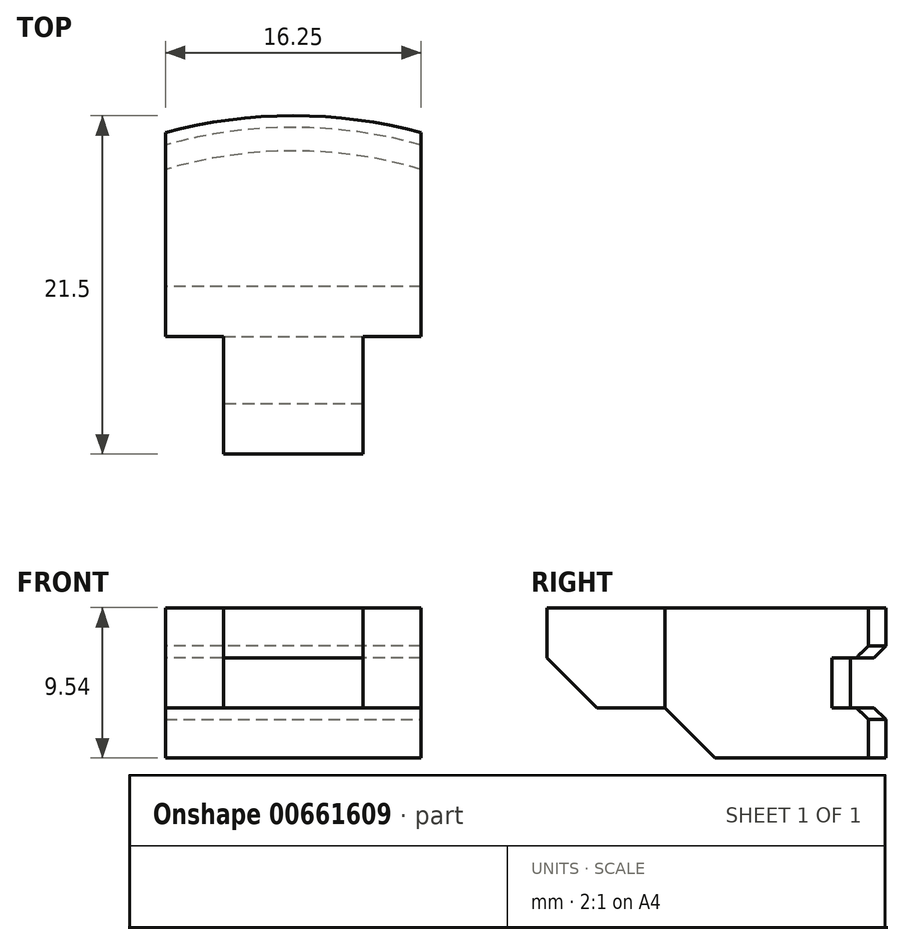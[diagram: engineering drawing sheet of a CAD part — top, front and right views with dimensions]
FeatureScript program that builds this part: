
annotation { "Feature Type Name" : "Feature", "Feature Type Description" : "" }
export const myFeature = defineFeature(function(context is Context, id is Id, definition is map)
    precondition{}
    {
        {
            var Q0;
            Q0=qCreatedBy(makeId("Top.planeOp"),FACE);
            var sketch = newSketch(context, id + "F0", { "sketchPlane" : qUnion([Q0])});
            skLineSegment(sketch, "E0.left", {"start": v(-8.12, 27.44) * mm, "end": v(-8.12, 16.84) * mm});
            skLineSegment(sketch, "E0.right", {"start": v(8.12, 27.44) * mm, "end": v(8.12, 16.84) * mm});
            skPoint(sketch, "E0.middle", {"position": v(0, 0) * mm});
            skArc(sketch, "E1", {"start": v(8.12, 27.44) * mm, "mid": v(0, 28.62) * mm, "end": v(-8.12, 27.44) * mm});
            skPoint(sketch, "E2.orphan", {"position": v(8.12, 28.62) * mm});
            skPoint(sketch, "E3.orphan", {"position": v(-8.12, 28.62) * mm});
            skPoint(sketch, "E4.orphan", {"position": v(-8.12, -28.62) * mm});
            skPoint(sketch, "E5.orphan", {"position": v(8.12, -28.62) * mm});
            skLineSegment(sketch, "E6.top", {"start": v(-8.12, 16.84) * mm, "end": v(8.12, 16.84) * mm});
            skLineSegment(sketch, "E7", {"start": v(0, 0) * mm, "end": v(0, 32.38) * mm, "construction": true});
            skPoint(sketch, "E7.endSnap0", {"position": v(0, 28.62) * mm});
            skLineSegment(sketch, "E8.bottom", {"start": v(4.43, 16.84) * mm, "end": v(0, 16.84) * mm});
            skLineSegment(sketch, "E8.top", {"start": v(4.43, 9.36) * mm, "end": v(0, 9.36) * mm});
            skLineSegment(sketch, "E8.left", {"start": v(4.43, 16.84) * mm, "end": v(4.43, 9.36) * mm});
            skLineSegment(sketch, "E8.right", {"start": v(0, 16.84) * mm, "end": v(0, 9.36) * mm});
            skLineSegment(sketch, "E9.MirrorCS", {"start": v(-4.43, 9.36) * mm, "end": v(0, 9.36) * mm});
            skLineSegment(sketch, "E10.MirrorCS", {"start": v(-4.43, 16.84) * mm, "end": v(-4.43, 9.36) * mm});
            skLineSegment(sketch, "E11.MirrorCS", {"start": v(8.12, 16.84) * mm, "end": v(-8.12, 16.84) * mm});
            skPoint(sketch, "E6.bottom.start.orphan", {"position": v(-8.12, -16.84) * mm});
            skPoint(sketch, "E12.trimOffspring.start.orphan", {"position": v(8.12, -16.84) * mm});
            skSolve(sketch);
        }
        {
            var Q0;
            Q0 = qSketchRegion(id + "F0", true);
            extrude(context, id + "F1", {"entities" : qUnion([Q0]), "oppositeDirection" : true, "depth" : 3.18 * mm, "offsetDistance" : 25 * mm});
        }
        {
            var Q0;
            Q0=makeQuery(id+"F0.imprint","IMPRINT",FACE,{"disambiguationData":[TD([[makeQuery(id+"F0.imprint","IMPRINT",EDGE,{"derivedFrom":sQuery(id+"F0.wireOp",EDGE,"E0.left")}),1.0]])]});
            var sketch = newSketch(context, id + "F2", { "sketchPlane" : qUnion([Q0])});
            skArc(sketch, "E13", {"start": v(8.1, 29.78) * mm, "mid": v(0, 30.86) * mm, "end": v(-8.13, 29.77) * mm});
            skLineSegment(sketch, "E14", {"start": v(-8.13, 27.45) * mm, "end": v(-8.13, 29.77) * mm});
            skLineSegment(sketch, "E15", {"start": v(8.1, 27.49) * mm, "end": v(8.1, 29.78) * mm});
            skLineSegment(sketch, "E16", {"start": v(-8.13, 27.45) * mm, "end": v(-8.13, 16.84) * mm});
            skLineSegment(sketch, "E17", {"start": v(-8.13, 16.84) * mm, "end": v(8.12, 16.84) * mm});
            skLineSegment(sketch, "E18", {"start": v(8.12, 16.84) * mm, "end": v(8.1, 27.49) * mm});
            skSolve(sketch);
        }
        {
            var Q0;
            Q0 = qSketchRegion(id + "F2", true);
            extrude(context, id + "F3", {"entities" : qUnion([Q0]), "operationType" : NewBodyOperationType.ADD, "depth" : 3.17 * mm, "offsetDistance" : 25 * mm});
        }
        {
            var Q0;
            Q0=qCreatedBy(makeId("Top.planeOp"),FACE);
            cPlane(context, id + "F4", {"entities" : qUnion([Q0]), "cplaneType" : CPlaneType.OFFSET, "offset" : 1.59 * mm, "oppositeDirection" : true, "width" : 150 * mm, "height" : 150 * mm});
        }
        {
            var Q0;
            Q0=makeQuery(id+"F1.opExtrude","SWEPT_BODY",BODY,{"disambiguationData":[OSD([sQuery(id+"F0.wireOp",EDGE,"E0.left"),sQuery(id+"F0.wireOp",EDGE,"E0.right"),sQuery(id+"F0.wireOp",EDGE,"E1"),sQuery(id+"F0.wireOp",EDGE,"E8.top"),sQuery(id+"F0.wireOp",EDGE,"E8.left"),sQuery(id+"F0.wireOp",EDGE,"E9.MirrorCS"),sQuery(id+"F0.wireOp",EDGE,"E10.MirrorCS"),sQuery(id+"F0.wireOp",EDGE,"E11.MirrorCS")])]});
            var Q1;
            Q1=qCreatedBy(id+"F4.planeOp",FACE);
            mirror(context, id + "F5", {"operationType" : NewBodyOperationType.ADD, "entities" : qUnion([Q0]), "mirrorPlane" : qUnion([Q1])});
        }
        {
            var Q0;
            Q0=makeQuery(id+"F5.opPattern","COPY",EDGE,{"derivedFrom":makeQuery(id+"F3.opExtrude","CAP_EDGE",EDGE,{"disambiguationData":[OSD([sQuery(id+"F2.wireOp",EDGE,"E13")])],"isStart":true}),"instanceName":"1"});
            var Q1;
            Q1=makeQuery(id+"F3.opExtrude","CAP_EDGE",EDGE,{"disambiguationData":[OSD([sQuery(id+"F2.wireOp",EDGE,"E13")])],"isStart":true});
            chamfer(context, id + "F6", {"entities" : qUnion([Q0, Q1]), "width" : .75 * mm, "tangentPropagation" : true});
        }
        {
            var Q0;
            {var subQ0=sQuery(id+"F0.wireOp",EDGE,"E8.right");Q0=makeQuery(id+"F0.imprint","IMPRINT",FACE,{"disambiguationData":[TD([[makeQuery(id+"F0.imprint","IMPRINT",EDGE,{"derivedFrom":subQ0}),-1.0]])]});}
            var sketch = newSketch(context, id + "F7", { "sketchPlane" : qUnion([Q0])});
            skLineSegment(sketch, "E19.bottom", {"start": v(-4.43, 16.84) * mm, "end": v(4.43, 16.84) * mm});
            skLineSegment(sketch, "E19.top", {"start": v(-4.43, 9.36) * mm, "end": v(4.43, 9.36) * mm});
            skLineSegment(sketch, "E19.left", {"start": v(-4.43, 16.84) * mm, "end": v(-4.43, 9.36) * mm});
            skLineSegment(sketch, "E19.right", {"start": v(4.43, 16.84) * mm, "end": v(4.43, 9.36) * mm});
            skSolve(sketch);
        }
        {
            var Q0;
            Q0 = qSketchRegion(id + "F7", true);
            extrude(context, id + "F8", {"entities" : qUnion([Q0]), "operationType" : NewBodyOperationType.ADD, "depth" : 3.17 * mm, "offsetDistance" : 25 * mm});
        }
        {
            var Q0;
            Q0=makeQuery(id+"F1.opExtrude","CAP_EDGE",EDGE,{"disambiguationData":[OSD([sQuery(id+"F0.wireOp",EDGE,"E8.top"),sQuery(id+"F0.wireOp",EDGE,"E9.MirrorCS")])],"isStart":false});
            var Q1;
            Q1=makeQuery(id+"F5.opPattern","COPY",EDGE,{"derivedFrom":makeQuery(id+"F3.opExtrude","CAP_EDGE",EDGE,{"disambiguationData":[OSD([sQuery(id+"F2.wireOp",EDGE,"E17")])],"isStart":false}),"instanceName":"1"});
            chamfer(context, id + "F9", {"entities" : qUnion([Q0, Q1]), "width" : 3.17 * mm, "tangentPropagation" : true});
        }
    });
